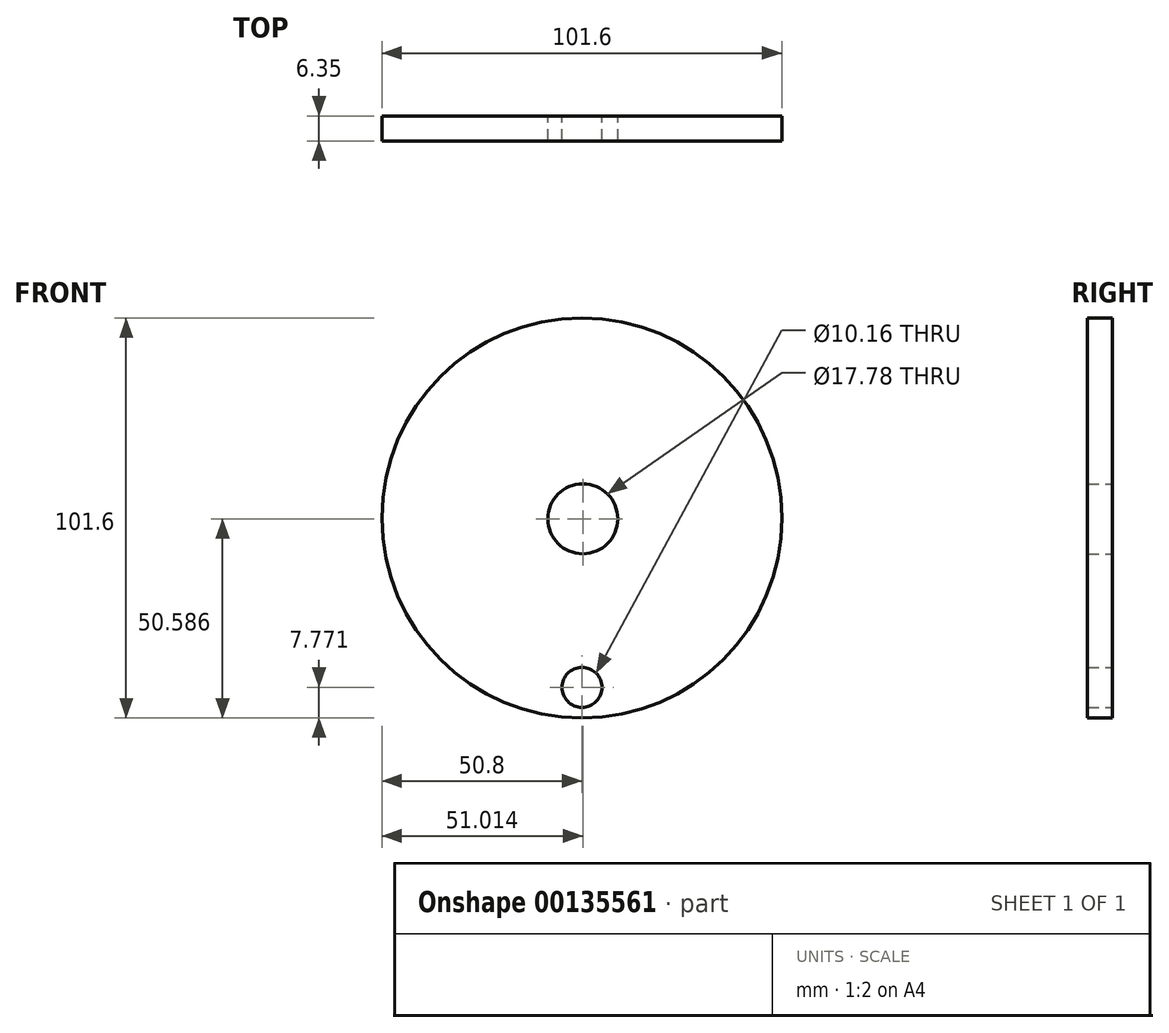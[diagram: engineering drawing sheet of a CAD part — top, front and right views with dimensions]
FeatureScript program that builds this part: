
annotation { "Feature Type Name" : "Feature", "Feature Type Description" : "" }
export const myFeature = defineFeature(function(context is Context, id is Id, definition is map)
    precondition{}
    {
        {
            var Q0;
            Q0=qCreatedBy(makeId("Front.planeOp"),FACE);
            var sketch = newSketch(context, id + "F0", { "sketchPlane" : qUnion([Q0])});
            skCircle(sketch, "E0", {"center": v(0, 0) * mm, "radius": 50.8 * mm});
            skCircle(sketch, "E1", {"center": v(0, -43.03) * mm, "radius": 5.08 * mm});
            skCircle(sketch, "E2", {"center": v(0.21, -0.21) * mm, "radius": 8.9 * mm});
            skSolve(sketch);
        }
        {
            var Q0;
            Q0 = qSketchRegion(id + "F0", true);
            extrude(context, id + "F1", {"entities" : qUnion([Q0]), "depth" : 6.35 * mm});
        }
    });
